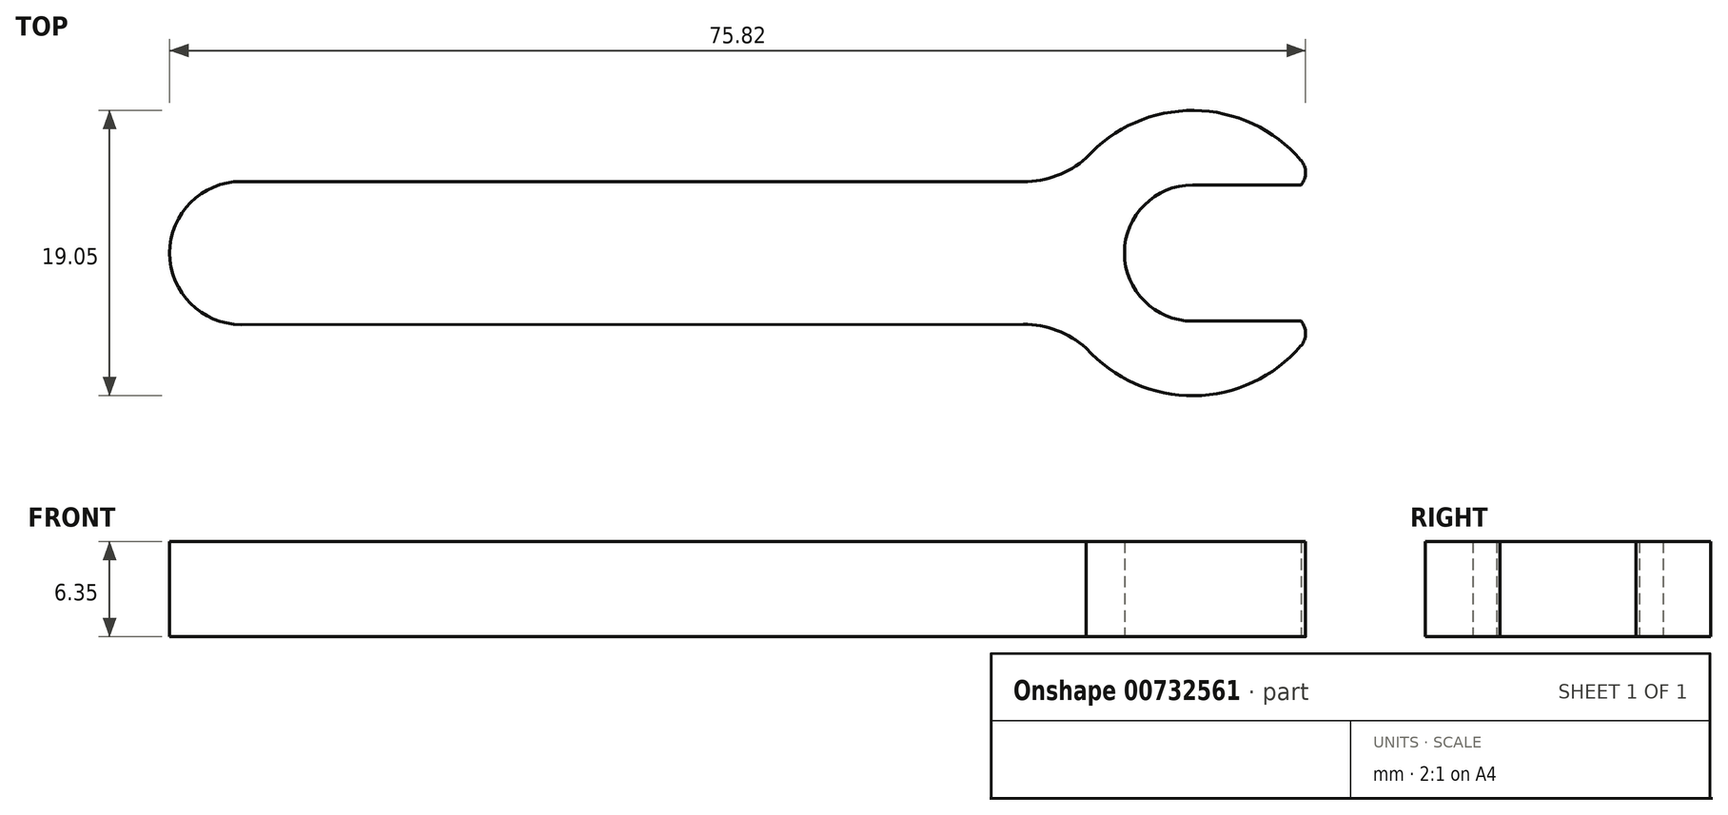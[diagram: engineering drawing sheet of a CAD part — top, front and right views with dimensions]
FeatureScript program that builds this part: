
annotation { "Feature Type Name" : "Feature", "Feature Type Description" : "" }
export const myFeature = defineFeature(function(context is Context, id is Id, definition is map)
    precondition{}
    {
        {
            var Q0;
            Q0=qCreatedBy(makeId("Top.planeOp"),FACE);
            var sketch = newSketch(context, id + "F0", { "sketchPlane" : qUnion([Q0])});
            skLineSegment(sketch, "E0", {"start": v(-31.75, 0) * mm, "end": v(31.75, 0) * mm, "construction": true});
            skArc(sketch, "E1", {"start": v(-31.75, 4.78) * mm, "mid": v(-36.53, 0) * mm, "end": v(-31.75, -4.78) * mm});
            skPoint(sketch, "E2", {"position": v(20.45, 4.76) * mm});
            skArc(sketch, "E3", {"start": v(38.98, 6.2) * mm, "mid": v(35.73, 8.65) * mm, "end": v(31.75, 9.53) * mm});
            skArc(sketch, "E4", {"start": v(38.98, 4.55) * mm, "mid": v(39.29, 5.37) * mm, "end": v(38.98, 6.2) * mm});
            skLineSegment(sketch, "E5", {"start": v(38.98, 4.55) * mm, "end": v(31.75, 4.55) * mm});
            skArc(sketch, "E6", {"start": v(31.75, 4.55) * mm, "mid": v(27.2, 0) * mm, "end": v(31.75, -4.55) * mm});
            skArc(sketch, "E7", {"start": v(31.75, 9.53) * mm, "mid": v(27.86, 8.7) * mm, "end": v(24.65, 6.34) * mm});
            skArc(sketch, "E8.MirrorCS", {"start": v(31.75, -9.53) * mm, "mid": v(27.86, -8.7) * mm, "end": v(24.65, -6.34) * mm});
            skArc(sketch, "E9.MirrorCS", {"start": v(38.98, -6.2) * mm, "mid": v(35.73, -8.65) * mm, "end": v(31.75, -9.53) * mm});
            skLineSegment(sketch, "E10.MirrorCS", {"start": v(38.98, -4.55) * mm, "end": v(31.75, -4.55) * mm});
            skArc(sketch, "E11.MirrorCS", {"start": v(38.98, -4.55) * mm, "mid": v(39.29, -5.37) * mm, "end": v(38.98, -6.2) * mm});
            skArc(sketch, "E12", {"start": v(20.45, 4.76) * mm, "mid": v(22.7, 5.17) * mm, "end": v(24.65, 6.34) * mm});
            skArc(sketch, "E13.MirrorCS", {"start": v(20.45, -4.76) * mm, "mid": v(22.7, -5.17) * mm, "end": v(24.65, -6.34) * mm});
            skLineSegment(sketch, "E14", {"start": v(-31.75, -4.78) * mm, "end": v(20.45, -4.76) * mm});
            skLineSegment(sketch, "E15", {"start": v(-31.75, -16.23) * mm, "end": v(-31.75, 16.68) * mm, "construction": true});
            skLineSegment(sketch, "E16", {"start": v(20.45, 4.76) * mm, "end": v(-31.75, 4.78) * mm});
            skSolve(sketch);
        }
        {
            var Q0;
            Q0=makeQuery(id+"F0.imprint","IMPRINT",FACE,{"disambiguationData":[TD([[makeQuery(id+"F0.imprint","IMPRINT",EDGE,{"derivedFrom":sQuery(id+"F0.wireOp",EDGE,"E1")}),1.0]])]});
            extrude(context, id + "F1", {"entities" : qUnion([Q0]), "depth" : 6.35 * mm, "offsetDistance" : 25.4 * mm});
        }
    });
